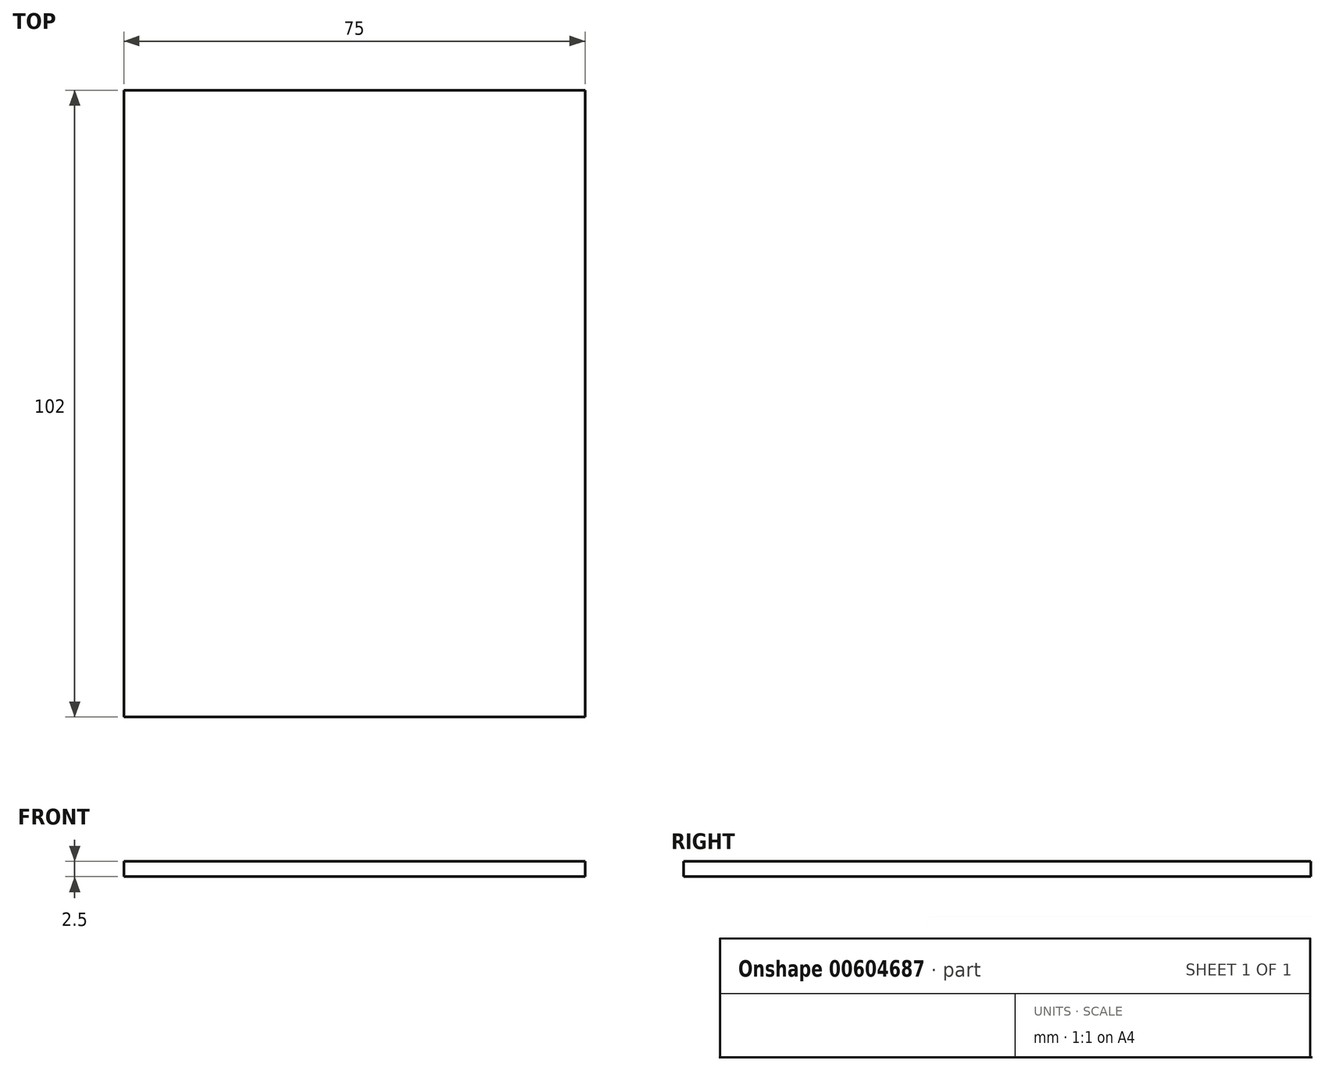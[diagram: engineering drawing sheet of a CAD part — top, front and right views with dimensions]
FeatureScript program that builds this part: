
annotation { "Feature Type Name" : "Feature", "Feature Type Description" : "" }
export const myFeature = defineFeature(function(context is Context, id is Id, definition is map)
    precondition{}
    {
        {
            var Q0;
            Q0=qCreatedBy(makeId("Top.planeOp"),FACE);
            var sketch = newSketch(context, id + "F0", { "sketchPlane" : qUnion([Q0])});
            skLineSegment(sketch, "E0.bottom", {"start": v(-55.24, 61.35) * mm, "end": v(19.76, 61.35) * mm});
            skLineSegment(sketch, "E0.top", {"start": v(-55.24, -40.65) * mm, "end": v(19.76, -40.65) * mm});
            skLineSegment(sketch, "E0.left", {"start": v(-55.24, 61.35) * mm, "end": v(-55.24, -40.65) * mm});
            skLineSegment(sketch, "E0.right", {"start": v(19.76, 61.35) * mm, "end": v(19.76, -40.65) * mm});
            skSolve(sketch);
        }
        {
            var Q0;
            Q0=makeQuery(id+"F0.imprint","IMPRINT",FACE,{"disambiguationData":[TD([[makeQuery(id+"F0.imprint","IMPRINT",EDGE,{"derivedFrom":sQuery(id+"F0.wireOp",EDGE,"E0.bottom")}),-1.0]])]});
            extrude(context, id + "F1", {"entities" : qUnion([Q0]), "depth" : 2.5 * mm, "offsetDistance" : 25 * mm});
        }
    });
